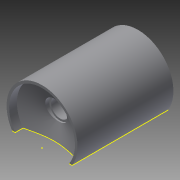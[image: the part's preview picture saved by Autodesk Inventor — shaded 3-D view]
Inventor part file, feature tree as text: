
AUTODESK INVENTOR PART (.ipt)
format: ipt  version: 2014 (Build 180170000, 170)  size: 598,528 bytes
history: native  units: mm
features: sketch x9, extrude x5, chamfer x3, plane x2, fillet x2, loft x1, projected_geometry x1
ambient origin geometry x8: Origin, YZ Plane, XZ Plane, XY Plane, X Axis, Y Axis, Z Axis, Center Point
bodies: Solid1 (feature_tree)
feature tree (23):
  extrude  "Extrusion1"  Depth=45.0mm
  sketch  "Sketch2"  dims[d2=55.0mm d3=5.0mm]
  plane  "Work Plane1"
  extrude  "Extrusion2"  Depth=5.0mm
  chamfer  "Chamfer1"  Distance=160.0mm
  sketch  "Sketch4"  dims[d7=70.0mm d8=-30.0mm]
  sketch  "Sketch5"  dims[d9=19.0mm d10=0.0mm d11=55.0mm d12=17.0mm d13=45.0deg]
  plane  "Work Plane2"
  extrude  "Extrusion3"  [1 undecoded]
  loft  "Loft1"
  extrude  "Extrusion4"  [1 undecoded]
  chamfer  "Chamfer2"  Distance=27.0mm
  extrude  "Extrusion5"  TaperAngle=0.0deg  [1 undecoded]
  chamfer  "Chamfer3"  Angle=90.0deg  [1 undecoded]
  fillet  "Fillet1"  Radius=10.0mm
  fillet  "Fillet2"  Radius=5.0mm
  sketch  "Sketch1"  dims[d0=90.0mm d1=45.0mm]
  sketch  "Sketch3"  dims[d4=5.0mm d5=160.0mm d6=0.0mm]
  projected_geometry  "Projected Loop1"
  sketch  "Sketch6"  dims[d14=33.0mm d15=-19.0mm]
  sketch  "Sketch7"  dims[d16=36.0mm d17=27.0mm d18=0.0mm]
  sketch  "Sketch8"  dims[d19=30.0mm d20=0.0mm d21=90.0deg d22=0.0mm d23=90.0deg d24=10.0mm d25=0.0mm]
  sketch  "Sketch9"  dims[d26=5.0mm d27=10.0mm d28=45.0deg d29=5.0mm d30=5.0mm d31=10.0mm d32=0.0mm d33=9.0mm d34=10.0mm d35=45.0deg d36=2.0mm d37=1.7mm]
note: 4 required parameter values undecoded (feature->parameter linkage not recoverable at this tier; creation-order binding heuristic only, values carry confidence <= 0.55)
